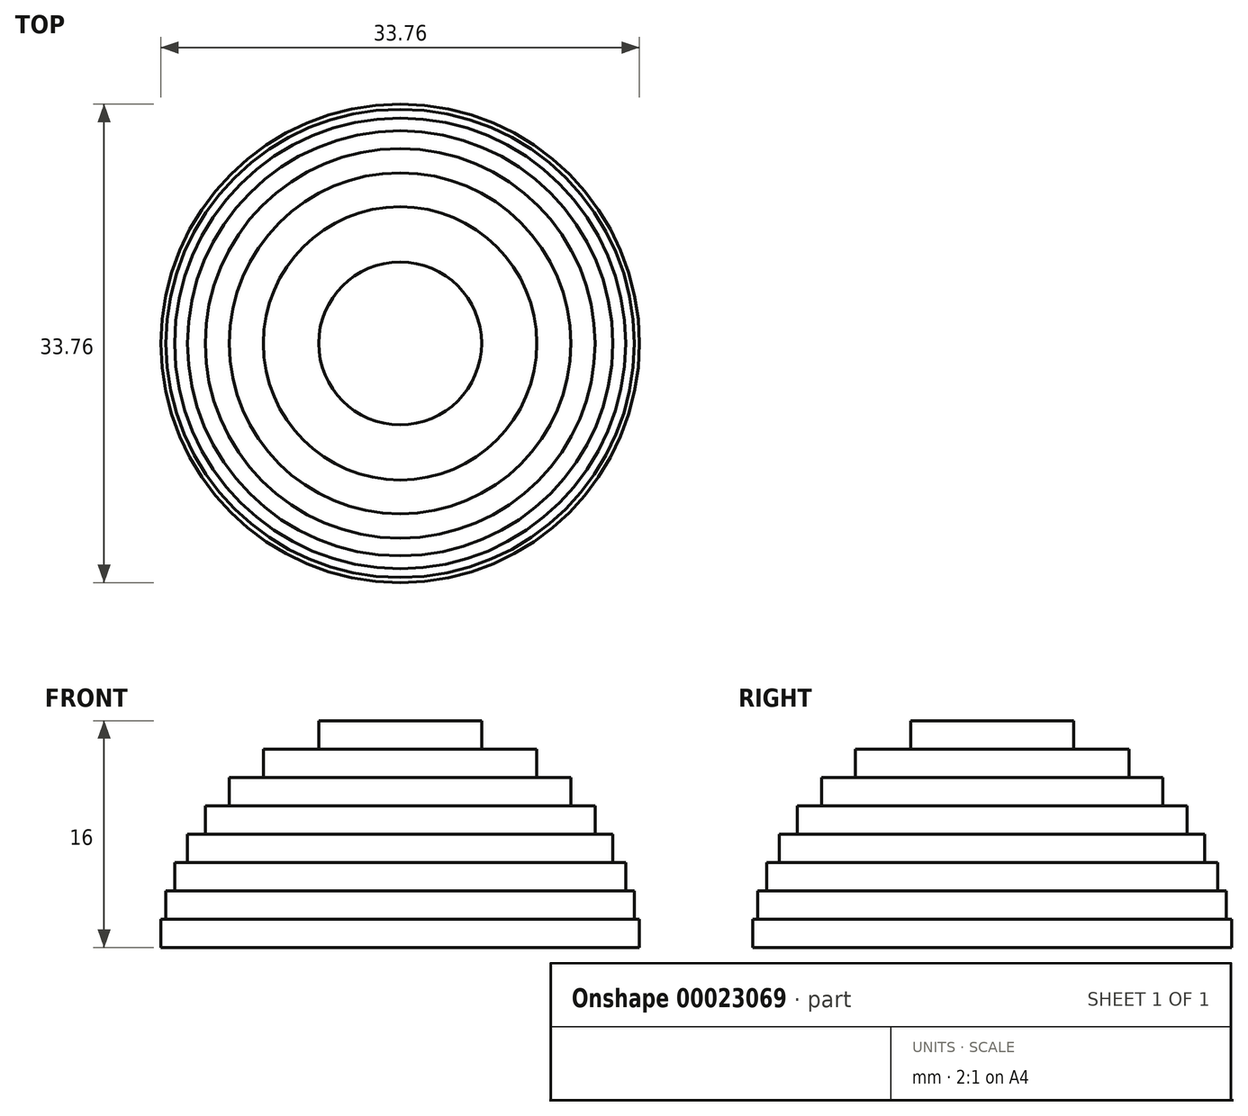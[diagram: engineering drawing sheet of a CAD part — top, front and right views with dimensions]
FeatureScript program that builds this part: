
annotation { "Feature Type Name" : "Feature", "Feature Type Description" : "" }
export const myFeature = defineFeature(function(context is Context, id is Id, definition is map)
    precondition{}
    {
        {
            var Q0;
            Q0=qCreatedBy(makeId("Front.planeOp"),FACE);
            var sketch = newSketch(context, id + "F0", { "sketchPlane" : qUnion([Q0])});
            skCircle(sketch, "E0", {"center": v(0, 0) * mm, "radius": 17 * mm, "construction": true});
            skLineSegment(sketch, "E1.bottom", {"start": v(-16.88, 2) * mm, "end": v(0, 2) * mm});
            skLineSegment(sketch, "E1.top", {"start": v(-16.88, 0) * mm, "end": v(0, 0) * mm});
            skLineSegment(sketch, "E1.left", {"start": v(-16.88, 2) * mm, "end": v(-16.88, 0) * mm});
            skLineSegment(sketch, "E1.right", {"start": v(0, 2) * mm, "end": v(0, 0) * mm});
            skLineSegment(sketch, "E2.bottom", {"start": v(-16.52, 4) * mm, "end": v(0, 4) * mm});
            skLineSegment(sketch, "E2.top", {"start": v(-16.52, 2) * mm, "end": v(0, 2) * mm});
            skLineSegment(sketch, "E2.left", {"start": v(-16.52, 4) * mm, "end": v(-16.52, 2) * mm});
            skLineSegment(sketch, "E2.right", {"start": v(0, 4) * mm, "end": v(0, 2) * mm});
            skLineSegment(sketch, "E3.bottom", {"start": v(-15.9, 6) * mm, "end": v(0, 6) * mm});
            skLineSegment(sketch, "E3.top", {"start": v(-15.9, 4) * mm, "end": v(0, 4) * mm});
            skLineSegment(sketch, "E3.left", {"start": v(-15.9, 6) * mm, "end": v(-15.9, 4) * mm});
            skLineSegment(sketch, "E3.right", {"start": v(0, 6) * mm, "end": v(0, 4) * mm});
            skLineSegment(sketch, "E4.bottom", {"start": v(-15, 8) * mm, "end": v(0, 8) * mm});
            skLineSegment(sketch, "E4.top", {"start": v(-15, 6) * mm, "end": v(0, 6) * mm});
            skLineSegment(sketch, "E4.left", {"start": v(-15, 8) * mm, "end": v(-15, 6) * mm});
            skLineSegment(sketch, "E4.right", {"start": v(0, 8) * mm, "end": v(0, 6) * mm});
            skLineSegment(sketch, "E5.bottom", {"start": v(-13.75, 10) * mm, "end": v(0, 10) * mm});
            skLineSegment(sketch, "E5.top", {"start": v(-13.75, 8) * mm, "end": v(0, 8) * mm});
            skLineSegment(sketch, "E5.left", {"start": v(-13.75, 10) * mm, "end": v(-13.75, 8) * mm});
            skLineSegment(sketch, "E5.right", {"start": v(0, 10) * mm, "end": v(0, 8) * mm});
            skLineSegment(sketch, "E6.bottom", {"start": v(-12.04, 12) * mm, "end": v(0, 12) * mm});
            skLineSegment(sketch, "E6.top", {"start": v(-12.04, 10) * mm, "end": v(0, 10) * mm});
            skLineSegment(sketch, "E6.left", {"start": v(-12.04, 12) * mm, "end": v(-12.04, 10) * mm});
            skLineSegment(sketch, "E6.right", {"start": v(0, 12) * mm, "end": v(0, 10) * mm});
            skLineSegment(sketch, "E7.bottom", {"start": v(-9.64, 14) * mm, "end": v(0, 14) * mm});
            skLineSegment(sketch, "E7.top", {"start": v(-9.64, 12) * mm, "end": v(0, 12) * mm});
            skLineSegment(sketch, "E7.left", {"start": v(-9.64, 14) * mm, "end": v(-9.64, 12) * mm});
            skLineSegment(sketch, "E7.right", {"start": v(0, 14) * mm, "end": v(0, 12) * mm});
            skLineSegment(sketch, "E8.bottom", {"start": v(-5.74, 16) * mm, "end": v(0, 16) * mm});
            skLineSegment(sketch, "E8.top", {"start": v(-5.74, 14) * mm, "end": v(0, 14) * mm});
            skLineSegment(sketch, "E8.left", {"start": v(-5.74, 16) * mm, "end": v(-5.74, 14) * mm});
            skLineSegment(sketch, "E8.right", {"start": v(0, 16) * mm, "end": v(0, 14) * mm});
            skLineSegment(sketch, "E9.bottom", {"start": v(0, 17) * mm, "end": v(0, 17) * mm});
            skLineSegment(sketch, "E9.top", {"start": v(0, 16) * mm, "end": v(0, 16) * mm});
            skLineSegment(sketch, "E9.left", {"start": v(0, 17) * mm, "end": v(0, 16) * mm});
            skSolve(sketch);
        }
        {
            var Q0;
            Q0=makeQuery(id+"F0.imprint","IMPRINT",FACE,{"disambiguationData":[TD([[makeQuery(id+"F0.imprint","IMPRINT",EDGE,{"derivedFrom":sQuery(id+"F0.wireOp",EDGE,"E8.bottom")}),-1.0]])]});
            var Q1;
            Q1=makeQuery(id+"F0.imprint","IMPRINT",FACE,{"disambiguationData":[TD([[makeQuery(id+"F0.imprint","IMPRINT",EDGE,{"derivedFrom":sQuery(id+"F0.wireOp",EDGE,"E7.bottom")}),-1.0]])]});
            var Q2;
            Q2=makeQuery(id+"F0.imprint","IMPRINT",FACE,{"disambiguationData":[TD([[makeQuery(id+"F0.imprint","IMPRINT",EDGE,{"derivedFrom":sQuery(id+"F0.wireOp",EDGE,"E6.bottom")}),-1.0]])]});
            var Q3;
            Q3=makeQuery(id+"F0.imprint","IMPRINT",FACE,{"disambiguationData":[TD([[makeQuery(id+"F0.imprint","IMPRINT",EDGE,{"derivedFrom":sQuery(id+"F0.wireOp",EDGE,"E5.bottom")}),-1.0]])]});
            var Q4;
            Q4=makeQuery(id+"F0.imprint","IMPRINT",FACE,{"disambiguationData":[TD([[makeQuery(id+"F0.imprint","IMPRINT",EDGE,{"derivedFrom":sQuery(id+"F0.wireOp",EDGE,"E4.bottom")}),-1.0]])]});
            var Q5;
            Q5=makeQuery(id+"F0.imprint","IMPRINT",FACE,{"disambiguationData":[TD([[makeQuery(id+"F0.imprint","IMPRINT",EDGE,{"derivedFrom":sQuery(id+"F0.wireOp",EDGE,"E3.bottom")}),-1.0]])]});
            var Q6;
            Q6=makeQuery(id+"F0.imprint","IMPRINT",FACE,{"disambiguationData":[TD([[makeQuery(id+"F0.imprint","IMPRINT",EDGE,{"derivedFrom":sQuery(id+"F0.wireOp",EDGE,"E2.bottom")}),-1.0]])]});
            var Q7;
            Q7=makeQuery(id+"F0.imprint","IMPRINT",FACE,{"disambiguationData":[TD([[makeQuery(id+"F0.imprint","IMPRINT",EDGE,{"derivedFrom":sQuery(id+"F0.wireOp",EDGE,"E1.bottom")}),-1.0]])]});
            var Q8;
            Q8=sQuery(id+"F0.wireOp",EDGE,"E1.right");
            revolve(context, id + "F1", {"entities" : qUnion([Q0, Q1, Q2, Q3, Q4, Q5, Q6, Q7]), "axis" : qUnion([Q8]), "revolveType" : RevolveType.FULL});
        }
    });
